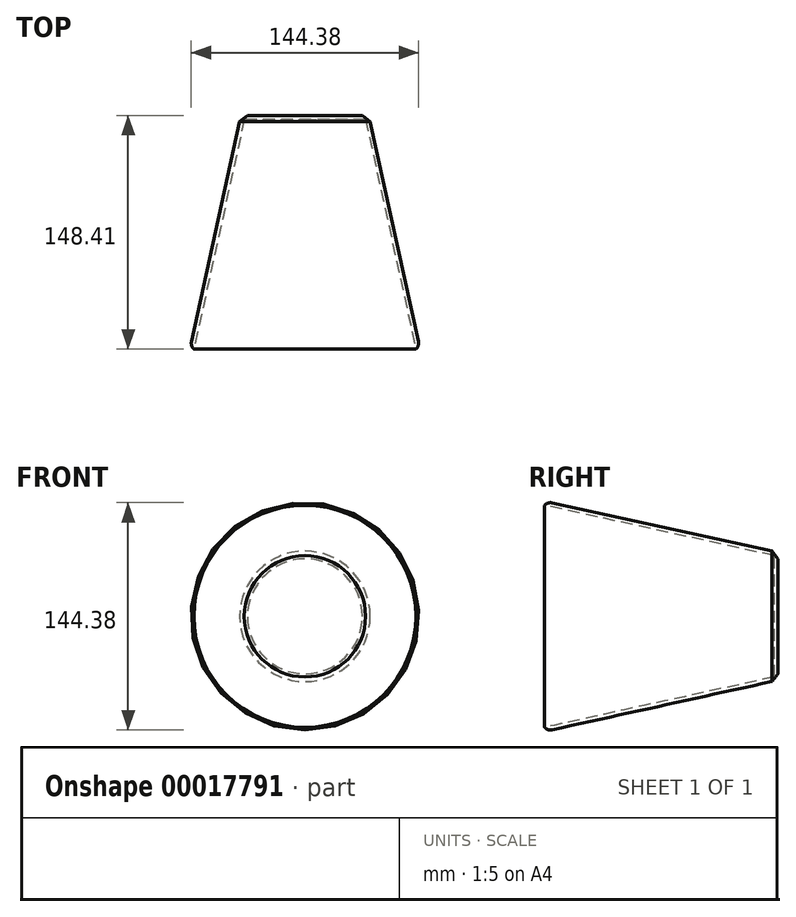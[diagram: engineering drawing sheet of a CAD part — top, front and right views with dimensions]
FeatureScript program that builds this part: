
annotation { "Feature Type Name" : "Feature", "Feature Type Description" : "" }
export const myFeature = defineFeature(function(context is Context, id is Id, definition is map)
    precondition{}
    {
        {
            var Q0;
            Q0=qCreatedBy(makeId("Front.planeOp"),FACE);
            var sketch = newSketch(context, id + "F0", { "sketchPlane" : qUnion([Q0])});
            skCircle(sketch, "E0", {"center": v(0, 0) * mm, "radius": 40.56 * mm});
            skSolve(sketch);
        }
        {
            var Q0;
            Q0=qCreatedBy(makeId("Front.planeOp"),FACE);
            cPlane(context, id + "F1", {"entities" : qUnion([Q0]), "cplaneType" : CPlaneType.OFFSET, "offset" : 152.4 * mm, "width" : 152.4 * mm, "height" : 152.4 * mm});
        }
        {
            var Q0;
            Q0=qCreatedBy(id+"F1.planeOp",FACE);
            var sketch = newSketch(context, id + "F2", { "sketchPlane" : qUnion([Q0])});
            skCircle(sketch, "E1", {"center": v(0, 0) * mm, "radius": 74 * mm});
            skSolve(sketch);
        }
        {
            var Q0;
            Q0=makeQuery(id+"F2.imprint","IMPRINT",FACE,{"disambiguationData":[TD([[makeQuery(id+"F2.imprint","IMPRINT",EDGE,{"derivedFrom":sQuery(id+"F2.wireOp",EDGE,"E1")}),1.0]])]});
            var Q1;
            Q1=makeQuery(id+"F0.imprint","IMPRINT",FACE,{"disambiguationData":[TD([[makeQuery(id+"F0.imprint","IMPRINT",EDGE,{"derivedFrom":sQuery(id+"F0.wireOp",EDGE,"E0")}),1.0]])]});
            loft(context, id + "F3", {"sheetProfilesArray" : [{ "sheetProfileEntities" : qUnion([Q0]) }, { "sheetProfileEntities" : qUnion([Q1]) }]});
        }
        {
            var Q0;
            Q0=makeQuery(id+"F3.opLoft","CAP_FACE",FACE,{"disambiguationData":[OSD([makeQuery(id+"F2.imprint","IMPRINT",FACE,{"disambiguationData":[TD([[makeQuery(id+"F2.imprint","IMPRINT",EDGE,{"derivedFrom":sQuery(id+"F2.wireOp",EDGE,"E1")}),1.0]])]})])],"isStart":true});
            shell(context, id + "F4", {"entities" : qUnion([Q0]), "thickness" : 2.54 * mm});
        }
        {
            var Q0;
            Q0=makeQuery(id+"F3.opLoft","MID_CAP_EDGE",EDGE,{"disambiguationData":[OSD([sQuery(id+"F0.wireOp",EDGE,"E0"),sQuery(id+"F2.wireOp",EDGE,"E1")])],"capPos":1.0});
            chamfer(context, id + "F5", {"entities" : qUnion([Q0]), "width" : 5.08 * mm, "tangentPropagation" : true});
        }
        {
            var Q0;
            Q0=makeQuery(id+"F4.opShell","OFFSET_EDGE",EDGE,{"disambiguationData":[OSD([sQuery(id+"F2.wireOp",EDGE,"E1")])]});
            chamfer(context, id + "F6", {"entities" : qUnion([Q0]), "width" : 5.08 * mm, "tangentPropagation" : true});
        }
        {
            var Q0;
            {var subQ0=sQuery(id+"F2.wireOp",EDGE,"E1");Q0=makeQuery(id+"F6.opChamfer","BLEND_EDGE",EDGE,{"blendedFrom":[makeQuery(id+"F4.opShell","OFFSET_EDGE",EDGE,{"disambiguationData":[OSD([subQ0])]}),makeQuery(id+"F3.opLoft","SWEPT_FACE",FACE,{"disambiguationData":[OSD([sQuery(id+"F0.wireOp",EDGE,"E0"),subQ0])]})],"blendedInto":[makeQuery(id+"F3.opLoft","SWEPT_FACE",FACE,{"disambiguationData":[OSD([sQuery(id+"F0.wireOp",EDGE,"E0"),subQ0])]})]});}
            fillet(context, id + "F7", {"entities" : qUnion([Q0]), "radius" : 5.08 * mm, "tangentPropagation" : true, "allowEdgeOverflow" : false});
        }
        {
            var Q0;
            Q0=qCreatedBy(makeId("Top.planeOp"),FACE);
            cPlane(context, id + "F8", {"entities" : qUnion([Q0]), "cplaneType" : CPlaneType.OFFSET, "offset" : 60.96 * mm, "oppositeDirection" : true, "width" : 152.4 * mm, "height" : 152.4 * mm});
        }
    });
